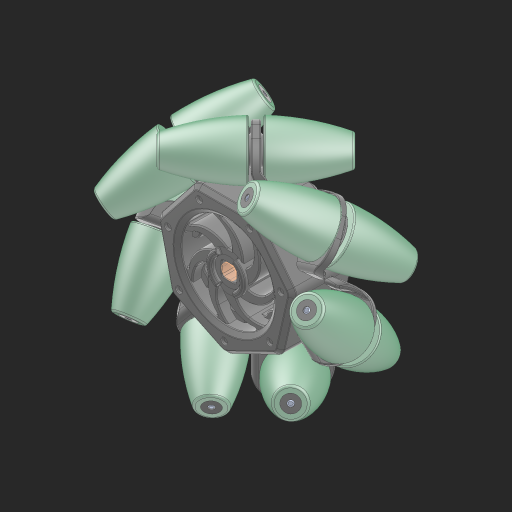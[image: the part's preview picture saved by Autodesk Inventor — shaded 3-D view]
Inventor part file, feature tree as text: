
AUTODESK INVENTOR PART (.ipt)
format: ipt  version: 2023 (Build 270158000, 158)  size: 16,492,032 bytes
history: native  units: in
note: dims shown in document units (in); Inventor stores cm internally (conversion verified against a paired STEP export)
features: other x48, sketch x1
ambient origin geometry x8: Origin, YZ Plane, XZ Plane, XY Plane, X Axis, Y Axis, Z Axis, Center Point
bodies: Solid1 (feature_tree), Solid2 (feature_tree), Solid3 (feature_tree), Solid4 (feature_tree), Solid5 (feature_tree), Solid6 (feature_tree), Solid7 (feature_tree), Solid8 (feature_tree), Solid9 (feature_tree), Solid10 (feature_tree), Solid11 (feature_tree), Solid12 (feature_tree), Solid13 (feature_tree), Solid14 (feature_tree), Solid15 (feature_tree), Solid16 (feature_tree), Solid17 (feature_tree), Solid18 (feature_tree), Solid19 (feature_tree), Solid20 (feature_tree), Solid21 (feature_tree), Solid22 (feature_tree), Solid23 (feature_tree), Solid24 (feature_tree), Solid25 (feature_tree), Solid26 (feature_tree), Solid27 (feature_tree), Solid28 (feature_tree), Solid29 (feature_tree), Solid30 (feature_tree), Solid31 (feature_tree), Solid32 (feature_tree), Solid33 (feature_tree), Solid34 (feature_tree), Solid35 (feature_tree), Solid36 (feature_tree), Solid37 (feature_tree), Solid38 (feature_tree), Solid39 (feature_tree), Solid40 (feature_tree), Solid41 (feature_tree), Solid42 (feature_tree), Solid43 (feature_tree), Solid44 (feature_tree)
feature tree (49):
  other  "4 Mecanum Right.ipt"
  other  "Solid1::4 Mecanum Right.ipt"
  other  "Solid2::4 Mecanum Right.ipt"
  other  "Solid3::4 Mecanum Right.ipt"
  other  "Solid4::4 Mecanum Right.ipt"
  other  "Solid5::4 Mecanum Right.ipt"
  other  "Solid6::4 Mecanum Right.ipt"
  other  "Solid7::4 Mecanum Right.ipt"
  other  "Solid8::4 Mecanum Right.ipt"
  other  "Solid9::4 Mecanum Right.ipt"
  other  "Solid10::4 Mecanum Right.ipt"
  other  "Solid11::4 Mecanum Right.ipt"
  other  "Solid12::4 Mecanum Right.ipt"
  other  "Solid13::4 Mecanum Right.ipt"
  other  "Solid14::4 Mecanum Right.ipt"
  other  "Solid15::4 Mecanum Right.ipt"
  other  "Solid16::4 Mecanum Right.ipt"
  other  "Solid17::4 Mecanum Right.ipt"
  other  "Solid18::4 Mecanum Right.ipt"
  other  "Solid19::4 Mecanum Right.ipt"
  other  "Solid20::4 Mecanum Right.ipt"
  other  "Solid21::4 Mecanum Right.ipt"
  other  "Solid22::4 Mecanum Right.ipt"
  other  "Solid23::4 Mecanum Right.ipt"
  other  "Solid24::4 Mecanum Right.ipt"
  other  "Solid25::4 Mecanum Right.ipt"
  other  "Solid26::4 Mecanum Right.ipt"
  other  "Solid27::4 Mecanum Right.ipt"
  other  "Solid28::4 Mecanum Right.ipt"
  other  "Solid29::4 Mecanum Right.ipt"
  other  "Solid30::4 Mecanum Right.ipt"
  other  "Solid31::4 Mecanum Right.ipt"
  other  "Solid32::4 Mecanum Right.ipt"
  other  "Solid33::4 Mecanum Right.ipt"
  other  "Solid34::4 Mecanum Right.ipt"
  other  "Solid35::4 Mecanum Right.ipt"
  other  "Solid36::4 Mecanum Right.ipt"
  other  "Solid37::4 Mecanum Right.ipt"
  other  "Solid38::4 Mecanum Right.ipt"
  other  "Solid39::4 Mecanum Right.ipt"
  other  "Solid40::4 Mecanum Right.ipt"
  other  "Solid41::4 Mecanum Right.ipt"
  other  "Solid42::4 Mecanum Right.ipt"
  other  "Solid43::4 Mecanum Right.ipt"
  other  "Solid44::4 Mecanum Right.ipt"
  other  "TaggingFeature1"
  sketch  "Sketch1"  dims[d0=0.3937in]
  other  "Srf1"
  other  "Srf1::Derived"
